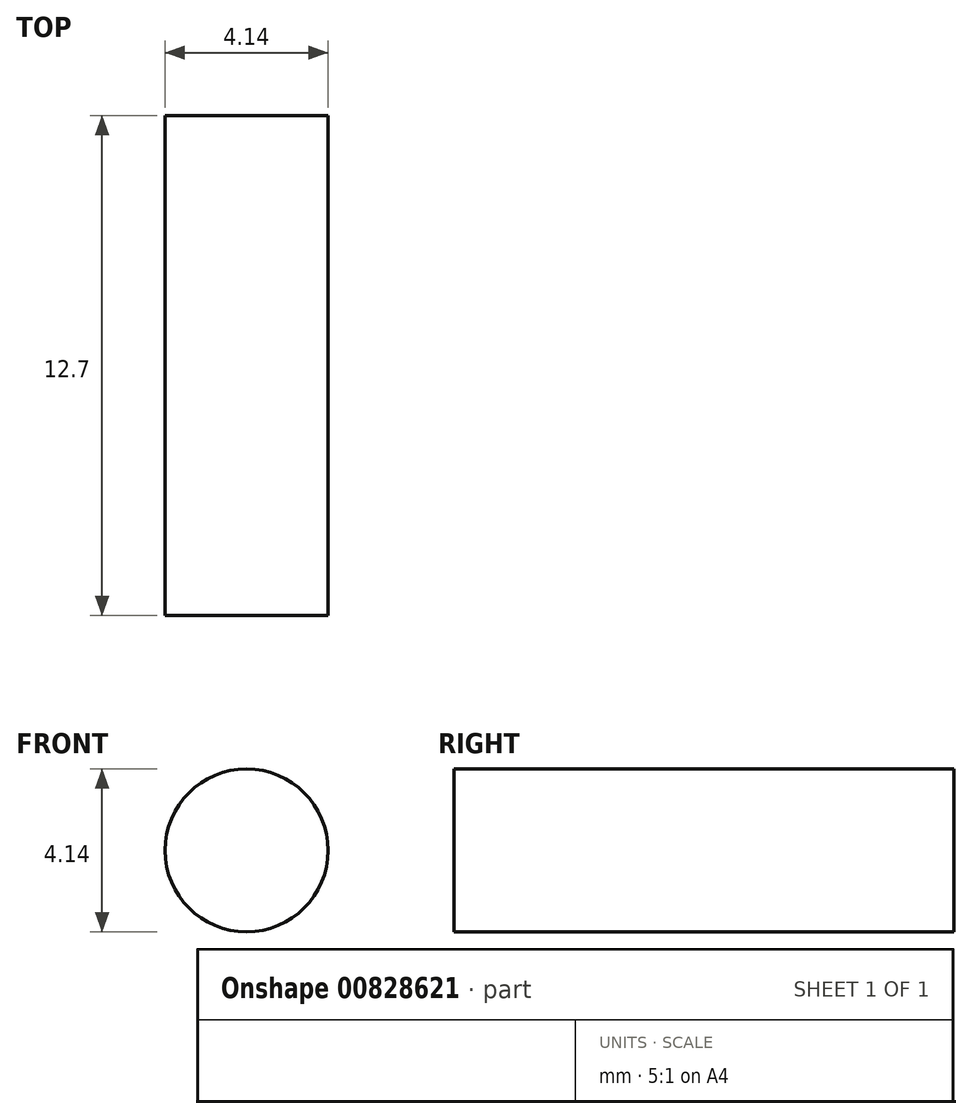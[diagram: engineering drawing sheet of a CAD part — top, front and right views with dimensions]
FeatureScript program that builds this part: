
annotation { "Feature Type Name" : "Feature", "Feature Type Description" : "" }
export const myFeature = defineFeature(function(context is Context, id is Id, definition is map)
    precondition{}
    {
        {
            var Q0;
            Q0=qCreatedBy(makeId("Front.planeOp"),FACE);
            var sketch = newSketch(context, id + "F0", { "sketchPlane" : qUnion([Q0])});
            skCircle(sketch, "E0", {"center": v(0, 0) * mm, "radius": 2.07 * mm});
            skSolve(sketch);
        }
        {
            var Q0;
            Q0 = qSketchRegion(id + "F0", true);
            extrude(context, id + "F1", {"entities" : qUnion([Q0]), "depth" : 12.7 * mm, "offsetDistance" : 25.4 * mm});
        }
    });
